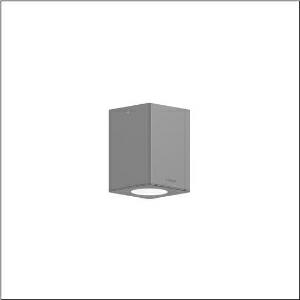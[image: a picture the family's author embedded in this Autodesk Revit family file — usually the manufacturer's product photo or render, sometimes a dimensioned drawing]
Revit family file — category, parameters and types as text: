
# Revit family: cl_31_decke_5cl613603
name_source: partatom
category: Lighting Fixtures
units: mm (PartAtom-declared; Revit-internal decimal feet)

## family parameters
Cut with Voids When Loaded = No
Host = Face
Light Source = No
Part Type = Normal
Room Calculation Point = No
Round Connector Dimension = Use Diameter
Shared = No

## types (1)
- --- (1 x LED, 1500 lm, 15 W, 3000K)
    Apparent Load = 15 VA
    CIE Flux Codes = 98 100 100 100 100
    Color Rendering = 80
    Color Temperature = 3000K
    Default Elevation = 1800 mm
    Description = CL 31 Ceiling, ceiling luminaire, primary light control with reflector, of aluminium, primary optical cover: cover panel, of glass, transparent, primary light characteristic: symmetric, installation type: surface-mounted, LED, rated luminous flux: 1.500lm, luminous efficacy: 100lm/W, light colour: 830, colour temperature: 3000K, control gear: ECG DALI, with terminal, 5-pole, max. 2.5mm², mains connection: 220..240V, AC, 50/60Hz, rated input power: 15W, luminaire housing, of aluminium, powder-coated, Siteco® metallic grey, length: 120mm, width: 120mm, height: 165mm, protection rating (complete): IP65, insulation class (complete): insulation class I (protective earthing), certification: CE, ENEC, impact resistance: IK09, permissible operating ambient temperature for outdoor applications: -20..+50°C, packaging unit: 1 piece
    Height = 166 mm
    Lamp = 1 x LED
    Lamp Light Flux = 1500 lm
    Lamp Power = 15 W
    Lamp count = 1
    Length = 120 mm
    Luminous efficacy = 100 lm/W
    Manufacturer = Siteco
    ModVariant = No
    Model = 5CL613603
    Mounting Place = Ceiling
    Mounting Type = Surface mounted
    Number of Poles = 1
    OnlyDefault = Yes
    Power Factor = 1
    Product Name = CL 31 Decke
    Product group = ceiling luminaire
    ProductGroupID = 304
    Protection Class = Protection class I
    Protection Degree = IP 65
    RLX_Detail_Level = 1
    RlxData = <blob elided: 33065 chars, md5=3b148ab4>
    Socket = socket
    Standby Power = 0 W
    System Light Flux = 1500 lm
    System Power = 15 W
    Type Comments = factory setting: luminous flux: 100 % | dim-lin: 254 | 348 mA
    Type Image = l_1006909.jpg
    URL = http://relux.com
    VarID = @adj_117211
    Voltage = 0 V
    Weight = 0.00 kg
    Width = 120 mm

## geometry (parser evidence)
native form markers: Blend x4, Sweep x11
no freeform markers — native parametric forms only
